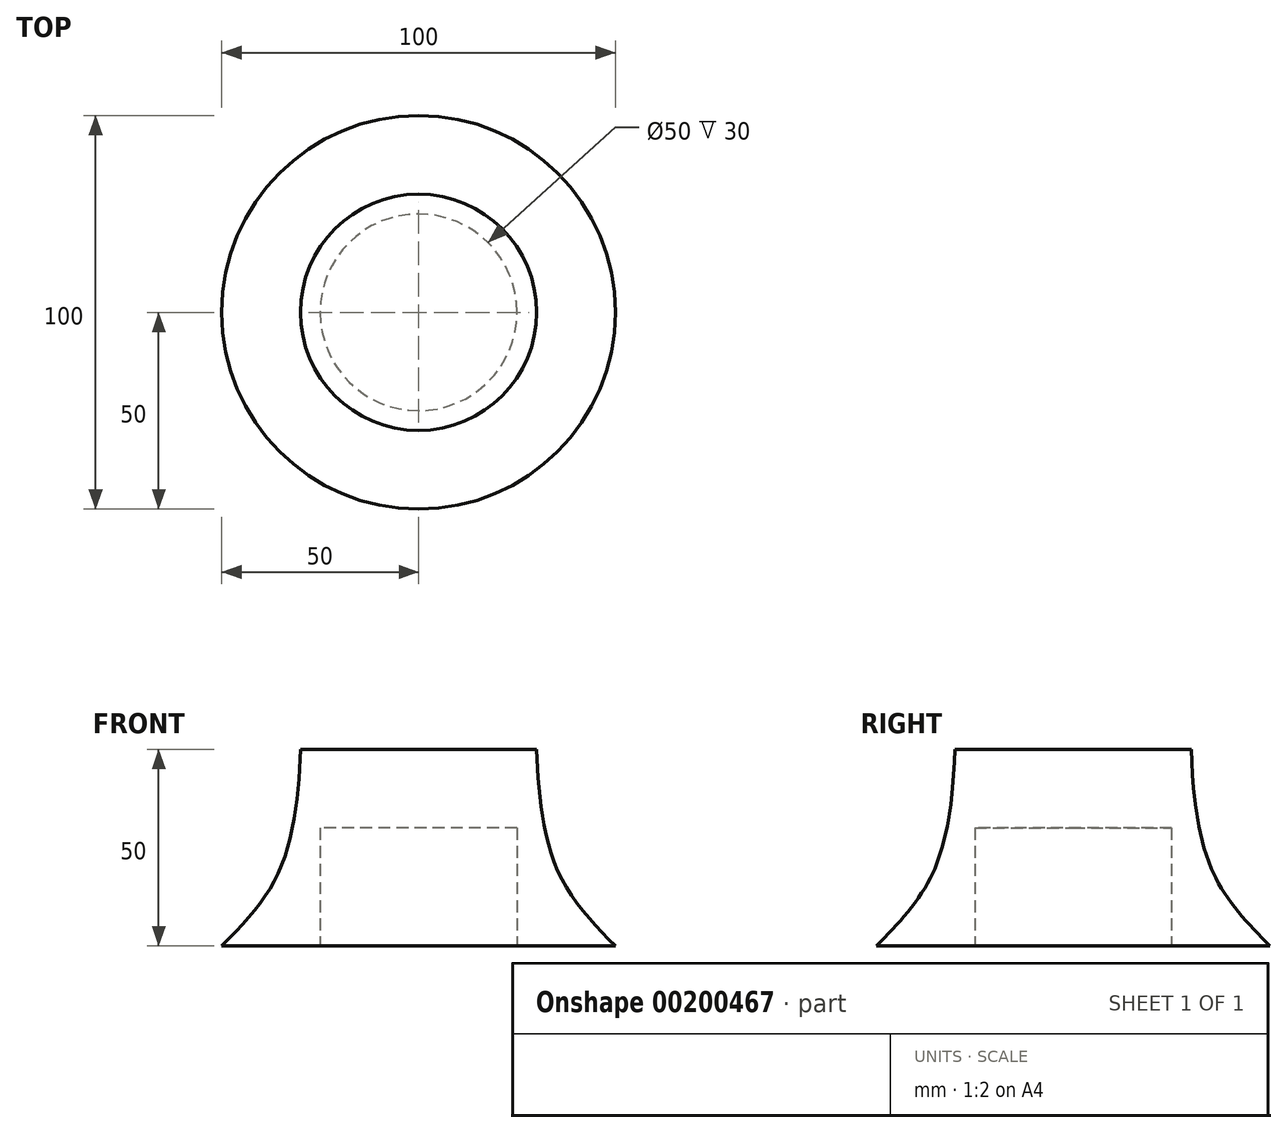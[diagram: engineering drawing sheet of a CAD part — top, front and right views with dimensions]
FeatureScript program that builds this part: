
annotation { "Feature Type Name" : "Feature", "Feature Type Description" : "" }
export const myFeature = defineFeature(function(context is Context, id is Id, definition is map)
    precondition{}
    {
        {
            var Q0;
            Q0=qCreatedBy(makeId("Front.planeOp"),FACE);
            var sketch = newSketch(context, id + "F0", { "sketchPlane" : qUnion([Q0])});
            skLineSegment(sketch, "E0", {"start": v(0, 0) * mm, "end": v(0, 50) * mm});
            skLineSegment(sketch, "E1", {"start": v(0, 0) * mm, "end": v(-50, 0) * mm});
            skLineSegment(sketch, "E2", {"start": v(0, 50) * mm, "end": v(-30, 50) * mm});
            skFitSpline(sketch, "E3", {"points": [v(-30, 50) * mm, v(-34.65, 20.79) * mm, v(-50, 0) * mm], "startDerivative": vector(-2.1, -55.93) * mm, "endDerivative": vector(-43.47, -44.2) * mm});
            skSolve(sketch);
        }
        {
            var Q0;
            Q0=makeQuery(id+"F0.imprint","IMPRINT",FACE,{"disambiguationData":[TD([[makeQuery(id+"F0.imprint","IMPRINT",EDGE,{"derivedFrom":sQuery(id+"F0.wireOp",EDGE,"E0")}),1.0]])]});
            var Q1;
            Q1=sQuery(id+"F0.wireOp",EDGE,"E0");
            revolve(context, id + "F1", {"entities" : qUnion([Q0]), "axis" : qUnion([Q1]), "revolveType" : RevolveType.FULL});
        }
        {
            var Q0;
            Q0=qCreatedBy(makeId("Top.planeOp"),FACE);
            var sketch = newSketch(context, id + "F2", { "sketchPlane" : qUnion([Q0])});
            skCircle(sketch, "E4", {"center": v(0, 0) * mm, "radius": 25 * mm});
            skSolve(sketch);
        }
        {
            var Q0;
            Q0 = qSketchRegion(id + "F2", true);
            extrude(context, id + "F3", {"entities" : qUnion([Q0]), "operationType" : NewBodyOperationType.REMOVE, "depth" : 30 * mm});
        }
    });
